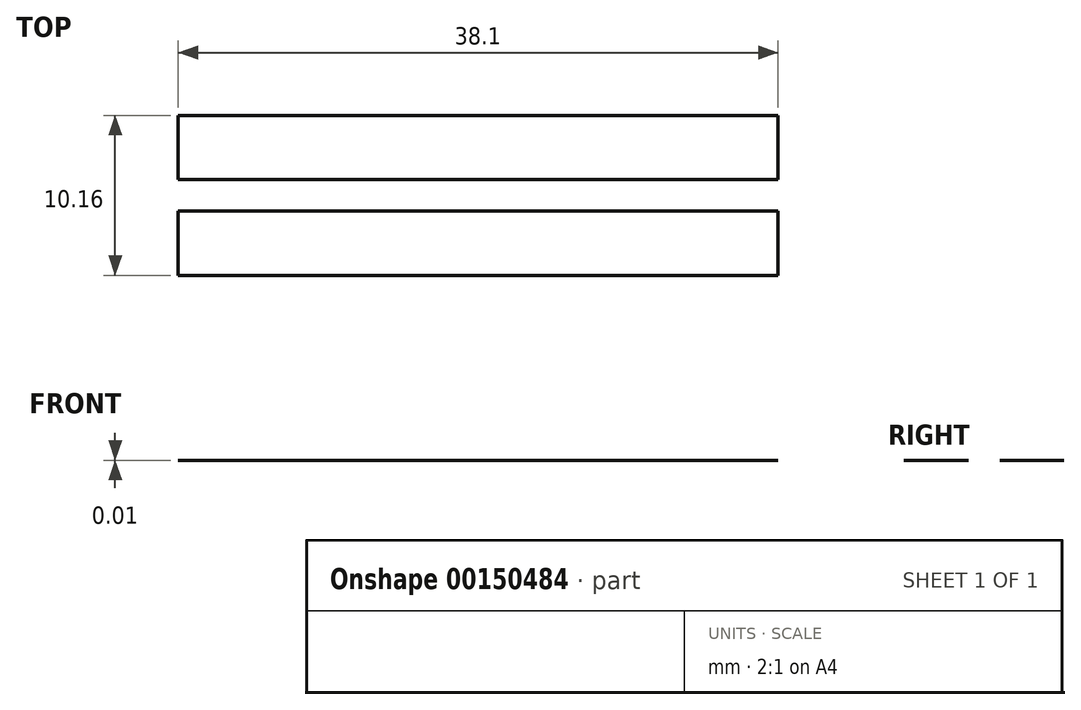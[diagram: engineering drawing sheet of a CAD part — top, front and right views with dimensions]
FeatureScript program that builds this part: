
annotation { "Feature Type Name" : "Feature", "Feature Type Description" : "" }
export const myFeature = defineFeature(function(context is Context, id is Id, definition is map)
    precondition{}
    {
        {
            var Q0;
            Q0=qCreatedBy(makeId("Top.planeOp"),FACE);
            var sketch = newSketch(context, id + "F0", { "sketchPlane" : qUnion([Q0])});
            skLineSegment(sketch, "E0.bottom", {"start": v(-19.05, 5.08) * mm, "end": v(19.05, 5.08) * mm});
            skLineSegment(sketch, "E0.top", {"start": v(-19.05, -5.08) * mm, "end": v(19.05, -5.08) * mm});
            skLineSegment(sketch, "E0.left", {"start": v(-19.05, 5.08) * mm, "end": v(-19.05, -5.08) * mm});
            skLineSegment(sketch, "E0.right", {"start": v(19.05, 5.08) * mm, "end": v(19.05, -5.08) * mm});
            skPoint(sketch, "E0.middle", {"position": v(0, 0) * mm});
            skSolve(sketch);
        }
        {
            var Q0;
            Q0=makeQuery(id+"F0.imprint","IMPRINT",FACE,{"disambiguationData":[TD([[makeQuery(id+"F0.imprint","IMPRINT",EDGE,{"derivedFrom":sQuery(id+"F0.wireOp",EDGE,"E0.bottom")}),-1.0]])]});
            extrude(context, id + "F1", {"entities" : qUnion([Q0]), "oppositeDirection" : true, "depth" : 3 / 203.2 * mm});
        }
        {
            var Q0;
            Q0=makeQuery(id+"F0.imprint","IMPRINT",FACE,{"disambiguationData":[TD([[makeQuery(id+"F0.imprint","IMPRINT",EDGE,{"derivedFrom":sQuery(id+"F0.wireOp",EDGE,"E0.bottom")}),-1.0]])]});
            var sketch = newSketch(context, id + "F2", { "sketchPlane" : qUnion([Q0])});
            skLineSegment(sketch, "E1.bottom", {"start": v(-19.05, 1) * mm, "end": v(19.05, 1) * mm});
            skLineSegment(sketch, "E1.top", {"start": v(-19.05, -1) * mm, "end": v(19.05, -1) * mm});
            skLineSegment(sketch, "E1.left", {"start": v(-19.05, 1) * mm, "end": v(-19.05, -1) * mm});
            skLineSegment(sketch, "E1.right", {"start": v(19.05, 1) * mm, "end": v(19.05, -1) * mm});
            skPoint(sketch, "E1.middle", {"position": v(0, 0) * mm});
            skSolve(sketch);
        }
        {
            var Q0;
            Q0 = qSketchRegion(id + "F2", true);
            extrude(context, id + "F3", {"entities" : qUnion([Q0]), "operationType" : NewBodyOperationType.REMOVE, "oppositeDirection" : true, "depth" : 1.27 * mm});
        }
    });
